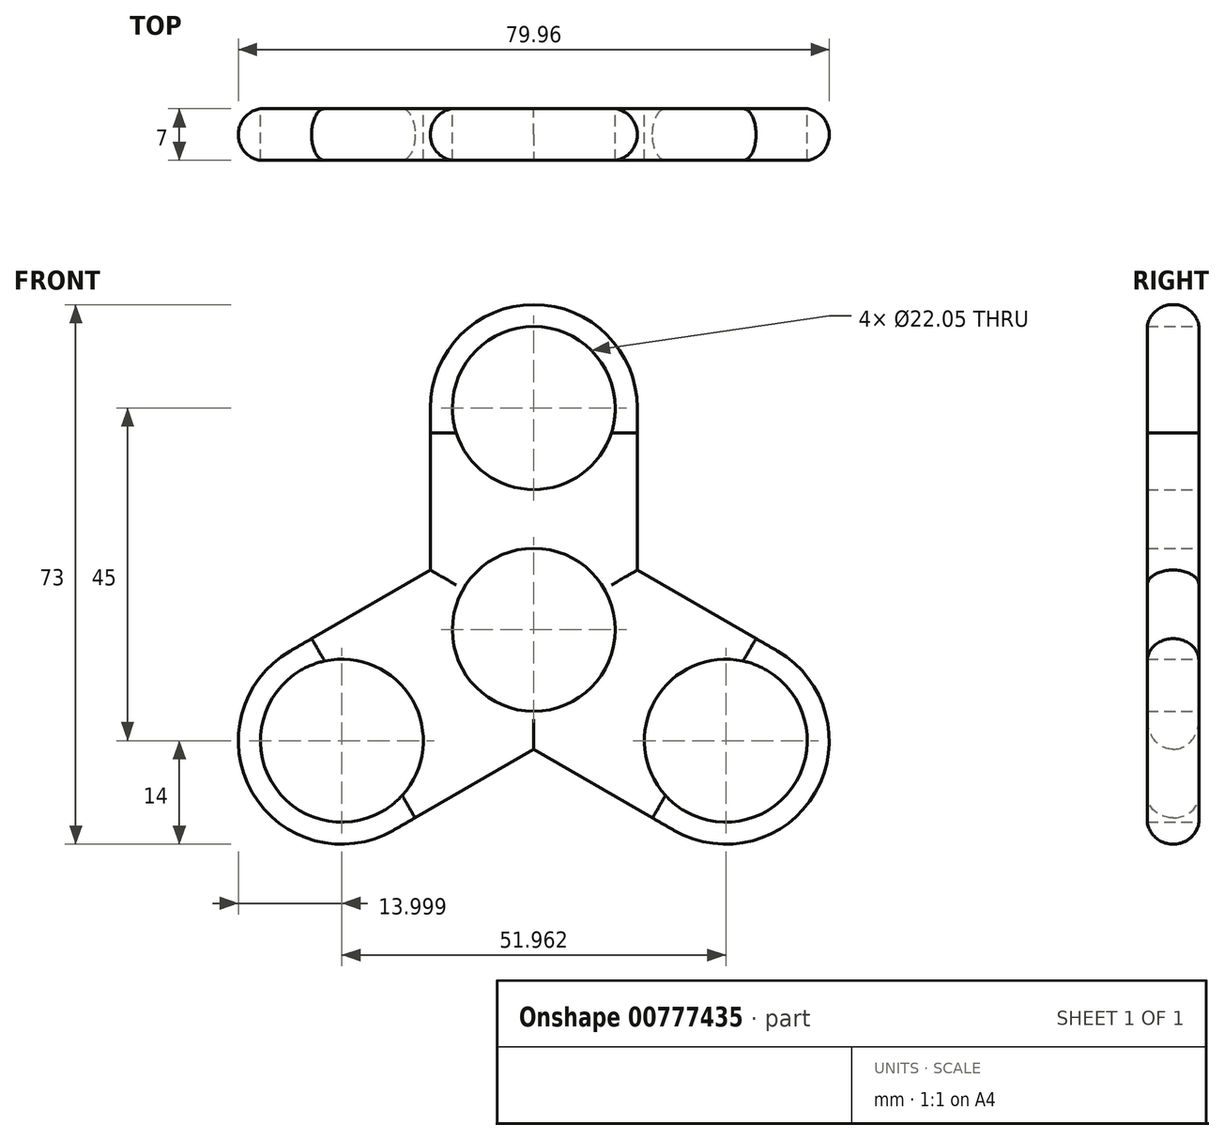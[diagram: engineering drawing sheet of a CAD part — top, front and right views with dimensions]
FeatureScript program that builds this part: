
annotation { "Feature Type Name" : "Feature", "Feature Type Description" : "" }
export const myFeature = defineFeature(function(context is Context, id is Id, definition is map)
    precondition{}
    {
        {
            var Q0;
            Q0=qCreatedBy(makeId("Front.planeOp"),FACE);
            var sketch = newSketch(context, id + "F0", { "sketchPlane" : qUnion([Q0])});
            skLineSegment(sketch, "E0.bottom", {"start": v(14, -15) * mm, "end": v(-14, -15) * mm});
            skLineSegment(sketch, "E0.top", {"start": v(14, 15) * mm, "end": v(-14, 15) * mm});
            skLineSegment(sketch, "E0.left", {"start": v(14, -15) * mm, "end": v(14, 15) * mm});
            skLineSegment(sketch, "E0.right", {"start": v(-14, -15) * mm, "end": v(-14, 15) * mm});
            skPoint(sketch, "E0.middle", {"position": v(0, 0) * mm});
            skCircle(sketch, "E1", {"center": v(0, 15) * mm, "radius": 14 * mm});
            skCircle(sketch, "E2", {"center": v(0, -15) * mm, "radius": 14 * mm});
            skCircle(sketch, "E3", {"center": v(0, 15) * mm, "radius": 11.03 * mm});
            skCircle(sketch, "E4", {"center": v(0, -15) * mm, "radius": 11.03 * mm});
            skSolve(sketch);
        }
        {
            var Q0;
            {var subQ1=sQuery(id+"F0.wireOp",EDGE,"E0.top");var subQ3=sQuery(id+"F0.wireOp",EDGE,"E3");var subQ4=makeQuery(id+"F0.imprint","INTERSECT",VERTEX,{"disambiguationData":[OD(0.0)],"derivedFrom":[subQ1,subQ3]});Q0=makeQuery(id+"F0.imprint","IMPRINT",FACE,{"disambiguationData":[TD([[makeQuery(id+"F0.imprint","IMPRINT",EDGE,{"disambiguationData":[TD([[subQ4,1.0]])],"derivedFrom":subQ3}),-1.0]])]});}
            var Q1;
            {var subQ1=sQuery(id+"F0.wireOp",EDGE,"E0.top");var subQ3=sQuery(id+"F0.wireOp",EDGE,"E3");var subQ4=makeQuery(id+"F0.imprint","INTERSECT",VERTEX,{"disambiguationData":[OD(0.0)],"derivedFrom":[subQ1,subQ3]});Q1=makeQuery(id+"F0.imprint","IMPRINT",FACE,{"disambiguationData":[TD([[makeQuery(id+"F0.imprint","IMPRINT",EDGE,{"disambiguationData":[TD([[subQ4,-1.0]])],"derivedFrom":subQ3}),-1.0]])]});}
            var Q2;
            {var subQ1=sQuery(id+"F0.wireOp",EDGE,"E0.bottom");var subQ3=sQuery(id+"F0.wireOp",EDGE,"E4");var subQ4=makeQuery(id+"F0.imprint","INTERSECT",VERTEX,{"disambiguationData":[OD(0.0)],"derivedFrom":[subQ1,subQ3]});Q2=makeQuery(id+"F0.imprint","IMPRINT",FACE,{"disambiguationData":[TD([[makeQuery(id+"F0.imprint","IMPRINT",EDGE,{"disambiguationData":[TD([[subQ4,1.0]])],"derivedFrom":subQ3}),-1.0]])]});}
            var Q3;
            {var subQ1=sQuery(id+"F0.wireOp",EDGE,"E0.bottom");var subQ3=sQuery(id+"F0.wireOp",EDGE,"E4");var subQ4=makeQuery(id+"F0.imprint","INTERSECT",VERTEX,{"disambiguationData":[OD(0.0)],"derivedFrom":[subQ1,subQ3]});Q3=makeQuery(id+"F0.imprint","IMPRINT",FACE,{"disambiguationData":[TD([[makeQuery(id+"F0.imprint","IMPRINT",EDGE,{"disambiguationData":[TD([[subQ4,-1.0]])],"derivedFrom":subQ3}),-1.0]])]});}
            var Q4;
            {var subQ0=sQuery(id+"F0.wireOp",EDGE,"E0.left");Q4=makeQuery(id+"F0.imprint","IMPRINT",FACE,{"disambiguationData":[TD([[makeQuery(id+"F0.imprint","IMPRINT",EDGE,{"derivedFrom":subQ0}),1.0]])]});}
            extrude(context, id + "F1", {"entities" : qUnion([Q0, Q1, Q2, Q3, Q4]), "depth" : 7 * mm, "offsetDistance" : 25.4 * mm});
        }
        {
            var Q0;
            Q0=makeQuery(id+"F1.opExtrude","SWEPT_BODY",BODY,{"disambiguationData":[OSD([sQuery(id+"F0.wireOp",EDGE,"E0.left"),sQuery(id+"F0.wireOp",EDGE,"E0.right"),sQuery(id+"F0.wireOp",EDGE,"E1"),sQuery(id+"F0.wireOp",EDGE,"E2"),sQuery(id+"F0.wireOp",EDGE,"E3"),sQuery(id+"F0.wireOp",EDGE,"E4")])]});
            var Q1;
            Q1=makeQuery(id+"F1.opExtrude","CAP_EDGE",EDGE,{"disambiguationData":[OSD([sQuery(id+"F0.wireOp",EDGE,"E4")])],"isStart":false});
            circularPattern(context, id + "F2", {"operationType" : NewBodyOperationType.ADD, "entities" : qUnion([Q0]), "axis" : qUnion([Q1]), "angle" : 360 * degree, "instanceCount" : 3, "equalSpace" : true});
        }
        {
            var Q0;
            Q0=makeQuery(id+"F1.opExtrude","CAP_EDGE",EDGE,{"disambiguationData":[OSD([sQuery(id+"F0.wireOp",EDGE,"E1")])],"isStart":false});
            var Q1;
            Q1=makeQuery(id+"F2.opPattern","COPY",EDGE,{"derivedFrom":makeQuery(id+"F1.opExtrude","CAP_EDGE",EDGE,{"disambiguationData":[OSD([sQuery(id+"F0.wireOp",EDGE,"E1")])],"isStart":false}),"instanceName":"4"});
            var Q2;
            Q2=makeQuery(id+"F2.opPattern","COPY",EDGE,{"derivedFrom":makeQuery(id+"F1.opExtrude","CAP_EDGE",EDGE,{"disambiguationData":[OSD([sQuery(id+"F0.wireOp",EDGE,"E0.right")])],"isStart":false}),"instanceName":"4"});
            var Q3;
            Q3=makeQuery(id+"F1.opExtrude","CAP_EDGE",EDGE,{"disambiguationData":[OSD([sQuery(id+"F0.wireOp",EDGE,"E0.left")])],"isStart":false});
            var Q4;
            Q4=makeQuery(id+"F1.opExtrude","CAP_EDGE",EDGE,{"disambiguationData":[OSD([sQuery(id+"F0.wireOp",EDGE,"E0.right")])],"isStart":false});
            var Q5;
            Q5=makeQuery(id+"F2.opPattern","COPY",EDGE,{"derivedFrom":makeQuery(id+"F1.opExtrude","CAP_EDGE",EDGE,{"disambiguationData":[OSD([sQuery(id+"F0.wireOp",EDGE,"E1")])],"isStart":false}),"instanceName":"1"});
            var Q6;
            Q6=makeQuery(id+"F2.opPattern","COPY",EDGE,{"derivedFrom":makeQuery(id+"F1.opExtrude","CAP_EDGE",EDGE,{"disambiguationData":[OSD([sQuery(id+"F0.wireOp",EDGE,"E0.left")])],"isStart":false}),"instanceName":"1"});
            var Q7;
            Q7=makeQuery(id+"F2.opPattern","COPY",EDGE,{"derivedFrom":makeQuery(id+"F1.opExtrude","CAP_EDGE",EDGE,{"disambiguationData":[OSD([sQuery(id+"F0.wireOp",EDGE,"E0.right")])],"isStart":false}),"instanceName":"1"});
            var Q8;
            Q8=makeQuery(id+"F2.opPattern","COPY",EDGE,{"derivedFrom":makeQuery(id+"F1.opExtrude","CAP_EDGE",EDGE,{"disambiguationData":[OSD([sQuery(id+"F0.wireOp",EDGE,"E0.left")])],"isStart":true}),"instanceName":"2"});
            var Q9;
            Q9=makeQuery(id+"F2.opPattern","COPY",EDGE,{"derivedFrom":makeQuery(id+"F1.opExtrude","CAP_EDGE",EDGE,{"disambiguationData":[OSD([sQuery(id+"F0.wireOp",EDGE,"E1")])],"isStart":false}),"instanceName":"2"});
            var Q10;
            Q10=makeQuery(id+"F2.opPattern","COPY",EDGE,{"derivedFrom":makeQuery(id+"F1.opExtrude","CAP_EDGE",EDGE,{"disambiguationData":[OSD([sQuery(id+"F0.wireOp",EDGE,"E0.right")])],"isStart":false}),"instanceName":"2"});
            var Q11;
            Q11=makeQuery(id+"F2.opPattern","COPY",EDGE,{"derivedFrom":makeQuery(id+"F1.opExtrude","CAP_EDGE",EDGE,{"disambiguationData":[OSD([sQuery(id+"F0.wireOp",EDGE,"E0.left")])],"isStart":false}),"instanceName":"3"});
            var Q12;
            Q12=makeQuery(id+"F2.opPattern","COPY",EDGE,{"derivedFrom":makeQuery(id+"F1.opExtrude","CAP_EDGE",EDGE,{"disambiguationData":[OSD([sQuery(id+"F0.wireOp",EDGE,"E0.right")])],"isStart":false}),"instanceName":"3"});
            fillet(context, id + "F3", {"entities" : qUnion([Q0, Q1, Q2, Q3, Q4, Q5, Q6, Q7, Q8, Q9, Q10, Q11, Q12]), "radius" : 3.5 * mm, "tangentPropagation" : true, "allowEdgeOverflow" : false});
        }
        {
            var Q0;
            Q0=makeQuery(id+"F1.opExtrude","CAP_EDGE",EDGE,{"disambiguationData":[OSD([sQuery(id+"F0.wireOp",EDGE,"E0.left")])],"isStart":true});
            var Q1;
            Q1=makeQuery(id+"F1.opExtrude","CAP_EDGE",EDGE,{"disambiguationData":[OSD([sQuery(id+"F0.wireOp",EDGE,"E1")])],"isStart":true});
            var Q2;
            Q2=makeQuery(id+"F2.opPattern","COPY",EDGE,{"derivedFrom":makeQuery(id+"F1.opExtrude","CAP_EDGE",EDGE,{"disambiguationData":[OSD([sQuery(id+"F0.wireOp",EDGE,"E0.left")])],"isStart":true}),"instanceName":"1"});
            var Q3;
            Q3=makeQuery(id+"F1.opExtrude","CAP_EDGE",EDGE,{"disambiguationData":[OSD([sQuery(id+"F0.wireOp",EDGE,"E0.right")])],"isStart":true});
            var Q4;
            Q4=makeQuery(id+"F2.opPattern","COPY",EDGE,{"derivedFrom":makeQuery(id+"F1.opExtrude","CAP_EDGE",EDGE,{"disambiguationData":[OSD([sQuery(id+"F0.wireOp",EDGE,"E1")])],"isStart":true}),"instanceName":"1"});
            var Q5;
            Q5=makeQuery(id+"F2.opPattern","COPY",EDGE,{"derivedFrom":makeQuery(id+"F1.opExtrude","CAP_EDGE",EDGE,{"disambiguationData":[OSD([sQuery(id+"F0.wireOp",EDGE,"E0.right")])],"isStart":true}),"instanceName":"1"});
            fillet(context, id + "F4", {"entities" : qUnion([Q0, Q1, Q2, Q3, Q4, Q5]), "radius" : 3.5 * mm, "tangentPropagation" : true, "allowEdgeOverflow" : false});
        }
    });
